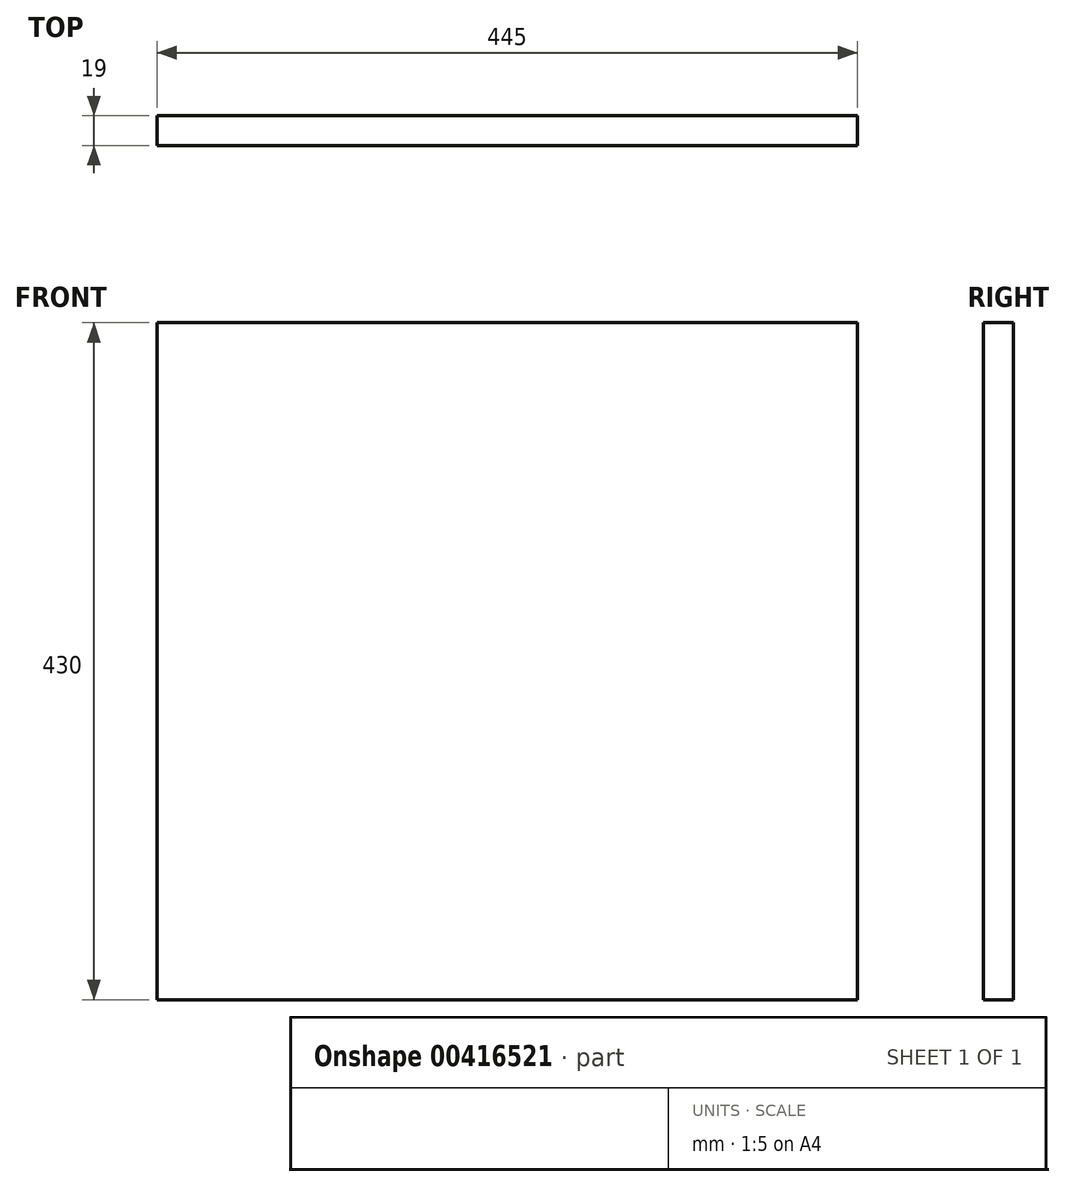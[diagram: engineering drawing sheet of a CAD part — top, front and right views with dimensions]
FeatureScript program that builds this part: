
annotation { "Feature Type Name" : "Feature", "Feature Type Description" : "" }
export const myFeature = defineFeature(function(context is Context, id is Id, definition is map)
    precondition{}
    {
        {
            var Q0;
            Q0=qCreatedBy(makeId("Front.planeOp"),FACE);
            var sketch = newSketch(context, id + "F0", { "sketchPlane" : qUnion([Q0])});
            skLineSegment(sketch, "E0.bottom", {"start": v(-222.5, 215) * mm, "end": v(222.5, 215) * mm});
            skLineSegment(sketch, "E0.top", {"start": v(-222.5, -215) * mm, "end": v(222.5, -215) * mm});
            skLineSegment(sketch, "E0.left", {"start": v(-222.5, 215) * mm, "end": v(-222.5, -215) * mm});
            skLineSegment(sketch, "E0.right", {"start": v(222.5, 215) * mm, "end": v(222.5, -215) * mm});
            skPoint(sketch, "E0.middle", {"position": v(0, 0) * mm});
            skSolve(sketch);
        }
        {
            var Q0;
            Q0 = qSketchRegion(id + "F0", true);
            extrude(context, id + "F1", {"entities" : qUnion([Q0]), "depth" : 19 * mm});
        }
    });
